# Revit family: Drywall_Suspension_System-USG-Curved_Ceilings-Vault
name_source: partatom
category: Specialty Equipment
revit_build: Autodesk Revit 2015 (Build: 20140905_0730(x64)
units: mm (PartAtom-declared; Revit-internal decimal feet)

## types (4) — shared parameters
ASTM C635 Duty Classification = 16 lb.
Accessories & Moldings = DGSC180, DGTC90, DGC4, DGC6, DGC8, DGWC, DGWC, DGSP180, DGHUB
Assembly Code = C3030200
Default Elevation = 0"
Description = Curved Main Tee
Fire Rating = Class A
Height = 1 1/2"
Installation Guide = https://www.usg.com
Manufacturer = USG
Notes = To hold down perimeter ceiling panels. Useful for maintaining Clean Room seal with US28CE molding.
Product Documentation Link = https://www.usg.com
Product Page URL = https://www.usg.com
Substrate = Metal - USG - Galvanized Steel
Type Comments = Vault
URL = www.usg.com
USG Item Number Note = "xxx" is a placeholder for a custom radius, in inches.
USG Literature = AC3118
Warranty = 30 years
Width = 1 1/2"

## per-type parameters (varying)
| type | DGW10VT | DGW12VT | DGW6VT | DGW8VT |
| DGW6VTxxx | No | No | Yes | No |
| DGW8VTxxx | No | No | No | Yes |
| DGW10VTxxx | Yes | No | No | No |
| DGW12VTxxx | No | Yes | No | No |

note: column(s) folded — value = type name in every type: Model, USG Item Number

## geometry (parser evidence)
native form markers: Sweep x3
no freeform markers — native parametric forms only
